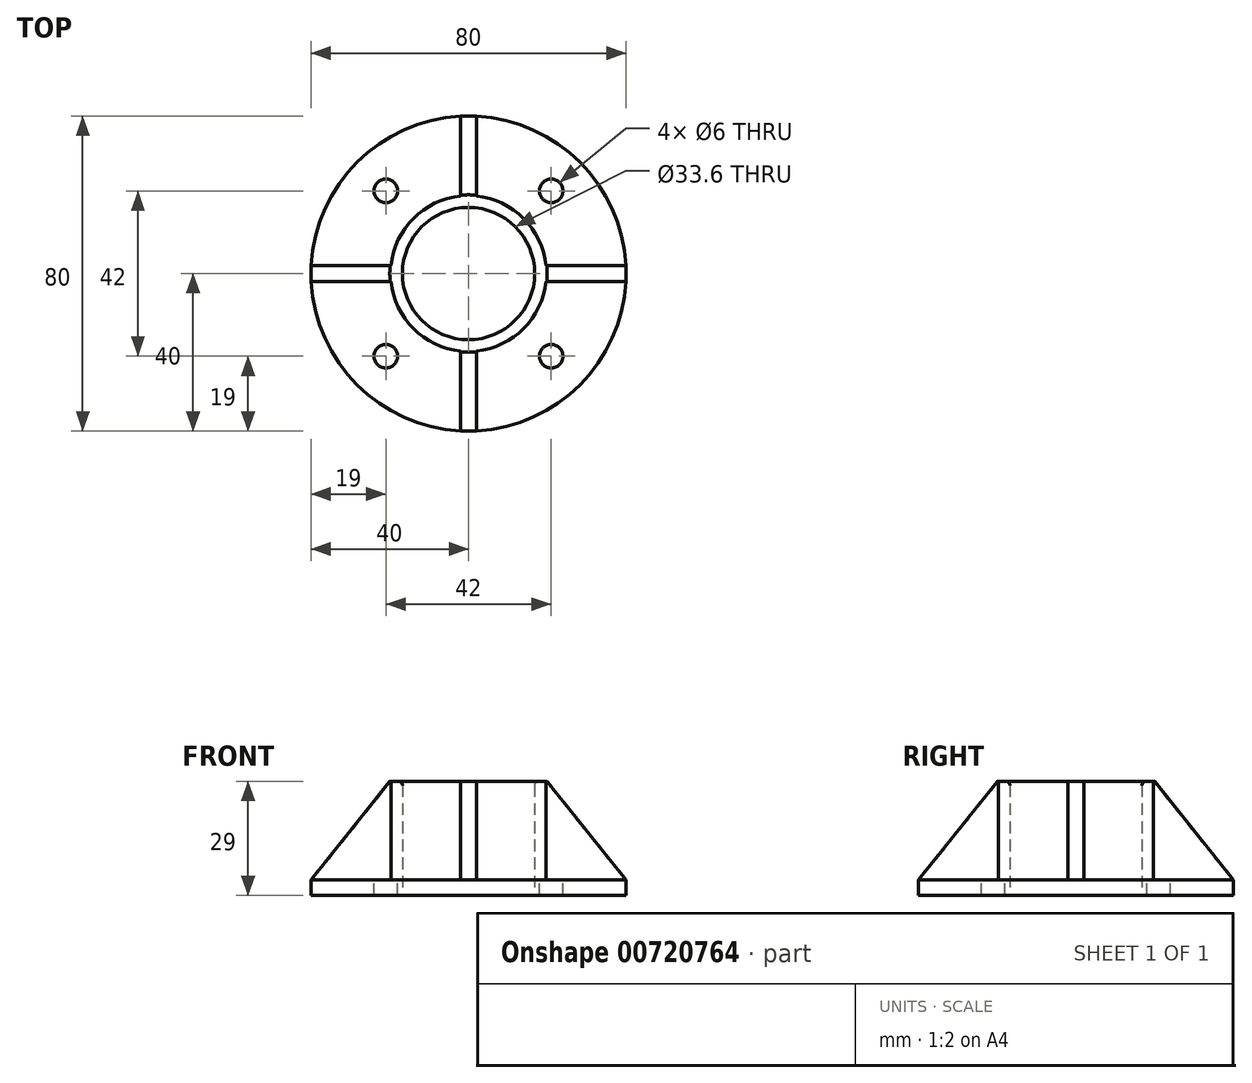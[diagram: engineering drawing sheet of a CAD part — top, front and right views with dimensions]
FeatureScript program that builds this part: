
annotation { "Feature Type Name" : "Feature", "Feature Type Description" : "" }
export const myFeature = defineFeature(function(context is Context, id is Id, definition is map)
    precondition{}
    {
        {
            var Q0;
            Q0=qCreatedBy(makeId("Top.planeOp"),FACE);
            var sketch = newSketch(context, id + "F0", { "sketchPlane" : qUnion([Q0])});
            skCircle(sketch, "E0", {"center": v(0, 0) * mm, "radius": 16.8 * mm});
            skCircle(sketch, "E1", {"center": v(0, 0) * mm, "radius": 19.8 * mm});
            skLineSegment(sketch, "E2.bottom", {"start": v(2, -40) * mm, "end": v(-2, -40) * mm});
            skLineSegment(sketch, "E2.top", {"start": v(2, 40) * mm, "end": v(-2, 40) * mm});
            skLineSegment(sketch, "E2.left", {"start": v(2, -40) * mm, "end": v(2, 40) * mm});
            skLineSegment(sketch, "E2.right", {"start": v(-2, -40) * mm, "end": v(-2, 40) * mm});
            skLineSegment(sketch, "E3.bottom", {"start": v(40, -2) * mm, "end": v(-40, -2) * mm});
            skLineSegment(sketch, "E3.top", {"start": v(40, 2) * mm, "end": v(-40, 2) * mm});
            skLineSegment(sketch, "E3.left", {"start": v(40, -2) * mm, "end": v(40, 2) * mm});
            skLineSegment(sketch, "E3.right", {"start": v(-40, -2) * mm, "end": v(-40, 2) * mm});
            skCircle(sketch, "E4", {"center": v(0, 0) * mm, "radius": 40 * mm});
            skLineSegment(sketch, "E5", {"start": v(-40, -2) * mm, "end": v(-2, -40) * mm, "construction": true});
            skLineSegment(sketch, "E6", {"start": v(2, -40) * mm, "end": v(40, -2) * mm, "construction": true});
            skLineSegment(sketch, "E7", {"start": v(40, 2) * mm, "end": v(2, 40) * mm, "construction": true});
            skLineSegment(sketch, "E8", {"start": v(-2, 40) * mm, "end": v(-40, 2) * mm, "construction": true});
            skCircle(sketch, "E9", {"center": v(21, 21) * mm, "radius": 3 * mm});
            skCircle(sketch, "E10", {"center": v(21, -21) * mm, "radius": 3 * mm});
            skCircle(sketch, "E11", {"center": v(-21, -21) * mm, "radius": 3 * mm});
            skCircle(sketch, "E12", {"center": v(-21, 21) * mm, "radius": 3 * mm});
            skSolve(sketch);
        }
        {
            var Q0;
            Q0=makeQuery(id+"F0.imprint","IMPRINT",FACE,{"disambiguationData":[TD([[makeQuery(id+"F0.imprint","IMPRINT",EDGE,{"derivedFrom":sQuery(id+"F0.wireOp",EDGE,"E0")}),-1.0]])]});
            var Q1;
            {var subQ1=sQuery(id+"F0.wireOp",EDGE,"E3.top");var subQ3=sQuery(id+"F0.wireOp",EDGE,"E1");var subQ4=makeQuery(id+"F0.imprint","INTERSECT",VERTEX,{"disambiguationData":[OD(1.0)],"derivedFrom":[subQ3,subQ1]});Q1=makeQuery(id+"F0.imprint","IMPRINT",FACE,{"disambiguationData":[TD([[makeQuery(id+"F0.imprint","IMPRINT",EDGE,{"disambiguationData":[TD([[subQ4,-1.0]])],"derivedFrom":subQ3}),-1.0]])]});}
            var Q2;
            {var subQ1=sQuery(id+"F0.wireOp",EDGE,"E2.right");var subQ3=sQuery(id+"F0.wireOp",EDGE,"E1");var subQ4=makeQuery(id+"F0.imprint","INTERSECT",VERTEX,{"disambiguationData":[OD(1.0)],"derivedFrom":[subQ3,subQ1]});Q2=makeQuery(id+"F0.imprint","IMPRINT",FACE,{"disambiguationData":[TD([[makeQuery(id+"F0.imprint","IMPRINT",EDGE,{"disambiguationData":[TD([[subQ4,-1.0]])],"derivedFrom":subQ3}),-1.0]])]});}
            var Q3;
            {var subQ1=sQuery(id+"F0.wireOp",EDGE,"E3.top");var subQ3=sQuery(id+"F0.wireOp",EDGE,"E1");var subQ4=makeQuery(id+"F0.imprint","INTERSECT",VERTEX,{"disambiguationData":[OD(0.0)],"derivedFrom":[subQ3,subQ1]});Q3=makeQuery(id+"F0.imprint","IMPRINT",FACE,{"disambiguationData":[TD([[makeQuery(id+"F0.imprint","IMPRINT",EDGE,{"disambiguationData":[TD([[subQ4,1.0]])],"derivedFrom":subQ3}),-1.0]])]});}
            var Q4;
            {var subQ3=sQuery(id+"F0.wireOp",EDGE,"E1");var subQ6=sQuery(id+"F0.wireOp",EDGE,"E2.left");var subQ8=makeQuery(id+"F0.imprint","INTERSECT",VERTEX,{"disambiguationData":[OD(0.0)],"derivedFrom":[subQ3,subQ6]});Q4=makeQuery(id+"F0.imprint","IMPRINT",FACE,{"disambiguationData":[TD([[makeQuery(id+"F0.imprint","IMPRINT",EDGE,{"disambiguationData":[TD([[subQ8,-1.0]])],"derivedFrom":subQ3}),-1.0]])]});}
            extrude(context, id + "F1", {"entities" : qUnion([Q0, Q1, Q2, Q3, Q4]), "depth" : 25 * mm, "offsetDistance" : 25 * mm});
        }
        {
            var Q0;
            Q0=makeQuery(id+"F0.imprint","IMPRINT",FACE,{"disambiguationData":[TD([[makeQuery(id+"F0.imprint","IMPRINT",EDGE,{"derivedFrom":sQuery(id+"F0.wireOp",EDGE,"E12")}),-1.0]])]});
            var Q1;
            Q1=makeQuery(id+"F0.imprint","IMPRINT",FACE,{"disambiguationData":[TD([[makeQuery(id+"F0.imprint","IMPRINT",EDGE,{"derivedFrom":sQuery(id+"F0.wireOp",EDGE,"E9")}),-1.0]])]});
            var Q2;
            {var subQ1=sQuery(id+"F0.wireOp",EDGE,"E3.top");var subQ3=sQuery(id+"F0.wireOp",EDGE,"E1");var subQ4=makeQuery(id+"F0.imprint","INTERSECT",VERTEX,{"disambiguationData":[OD(0.0)],"derivedFrom":[subQ3,subQ1]});Q2=makeQuery(id+"F0.imprint","IMPRINT",FACE,{"disambiguationData":[TD([[makeQuery(id+"F0.imprint","IMPRINT",EDGE,{"disambiguationData":[TD([[subQ4,1.0]])],"derivedFrom":subQ3}),-1.0]])]});}
            var Q3;
            {var subQ3=sQuery(id+"F0.wireOp",EDGE,"E1");var subQ6=sQuery(id+"F0.wireOp",EDGE,"E2.left");var subQ8=makeQuery(id+"F0.imprint","INTERSECT",VERTEX,{"disambiguationData":[OD(0.0)],"derivedFrom":[subQ3,subQ6]});Q3=makeQuery(id+"F0.imprint","IMPRINT",FACE,{"disambiguationData":[TD([[makeQuery(id+"F0.imprint","IMPRINT",EDGE,{"disambiguationData":[TD([[subQ8,-1.0]])],"derivedFrom":subQ3}),-1.0]])]});}
            var Q4;
            Q4=makeQuery(id+"F0.imprint","IMPRINT",FACE,{"disambiguationData":[TD([[makeQuery(id+"F0.imprint","IMPRINT",EDGE,{"derivedFrom":sQuery(id+"F0.wireOp",EDGE,"E10")}),-1.0]])]});
            var Q5;
            {var subQ0=sQuery(id+"F0.wireOp",EDGE,"E2.left");var subQ1=sQuery(id+"F0.wireOp",EDGE,"E0");var subQ2=makeQuery(id+"F0.imprint","INTERSECT",VERTEX,{"disambiguationData":[OD(1.0)],"derivedFrom":[subQ1,subQ0]});Q5=makeQuery(id+"F0.imprint","IMPRINT",FACE,{"disambiguationData":[TD([[makeQuery(id+"F0.imprint","IMPRINT",EDGE,{"disambiguationData":[TD([[subQ2,-1.0]])],"derivedFrom":subQ1}),-1.0]])]});}
            var Q6;
            {var subQ0=sQuery(id+"F0.wireOp",EDGE,"E3.top");var subQ1=sQuery(id+"F0.wireOp",EDGE,"E0");var subQ2=makeQuery(id+"F0.imprint","INTERSECT",VERTEX,{"disambiguationData":[OD(0.0)],"derivedFrom":[subQ1,subQ0]});Q6=makeQuery(id+"F0.imprint","IMPRINT",FACE,{"disambiguationData":[TD([[makeQuery(id+"F0.imprint","IMPRINT",EDGE,{"disambiguationData":[TD([[subQ2,1.0]])],"derivedFrom":subQ1}),-1.0]])]});}
            var Q7;
            {var subQ0=sQuery(id+"F0.wireOp",EDGE,"E2.left");var subQ1=sQuery(id+"F0.wireOp",EDGE,"E0");var subQ2=makeQuery(id+"F0.imprint","INTERSECT",VERTEX,{"disambiguationData":[OD(0.0)],"derivedFrom":[subQ1,subQ0]});Q7=makeQuery(id+"F0.imprint","IMPRINT",FACE,{"disambiguationData":[TD([[makeQuery(id+"F0.imprint","IMPRINT",EDGE,{"disambiguationData":[TD([[subQ2,1.0]])],"derivedFrom":subQ1}),-1.0]])]});}
            var Q8;
            {var subQ0=sQuery(id+"F0.wireOp",EDGE,"E2.right");var subQ1=sQuery(id+"F0.wireOp",EDGE,"E0");var subQ2=makeQuery(id+"F0.imprint","INTERSECT",VERTEX,{"disambiguationData":[OD(1.0)],"derivedFrom":[subQ1,subQ0]});Q8=makeQuery(id+"F0.imprint","IMPRINT",FACE,{"disambiguationData":[TD([[makeQuery(id+"F0.imprint","IMPRINT",EDGE,{"disambiguationData":[TD([[subQ2,-1.0]])],"derivedFrom":subQ1}),-1.0]])]});}
            var Q9;
            {var subQ1=sQuery(id+"F0.wireOp",EDGE,"E2.right");var subQ3=sQuery(id+"F0.wireOp",EDGE,"E1");var subQ4=makeQuery(id+"F0.imprint","INTERSECT",VERTEX,{"disambiguationData":[OD(1.0)],"derivedFrom":[subQ3,subQ1]});Q9=makeQuery(id+"F0.imprint","IMPRINT",FACE,{"disambiguationData":[TD([[makeQuery(id+"F0.imprint","IMPRINT",EDGE,{"disambiguationData":[TD([[subQ4,-1.0]])],"derivedFrom":subQ3}),-1.0]])]});}
            var Q10;
            {var subQ0=sQuery(id+"F0.wireOp",EDGE,"E3.bottom");var subQ1=sQuery(id+"F0.wireOp",EDGE,"E0");var subQ2=makeQuery(id+"F0.imprint","INTERSECT",VERTEX,{"disambiguationData":[OD(0.0)],"derivedFrom":[subQ1,subQ0]});Q10=makeQuery(id+"F0.imprint","IMPRINT",FACE,{"disambiguationData":[TD([[makeQuery(id+"F0.imprint","IMPRINT",EDGE,{"disambiguationData":[TD([[subQ2,-1.0]])],"derivedFrom":subQ1}),-1.0]])]});}
            var Q11;
            Q11=makeQuery(id+"F0.imprint","IMPRINT",FACE,{"disambiguationData":[TD([[makeQuery(id+"F0.imprint","IMPRINT",EDGE,{"derivedFrom":sQuery(id+"F0.wireOp",EDGE,"E11")}),-1.0]])]});
            var Q12;
            {var subQ1=sQuery(id+"F0.wireOp",EDGE,"E3.top");var subQ3=sQuery(id+"F0.wireOp",EDGE,"E1");var subQ4=makeQuery(id+"F0.imprint","INTERSECT",VERTEX,{"disambiguationData":[OD(1.0)],"derivedFrom":[subQ3,subQ1]});Q12=makeQuery(id+"F0.imprint","IMPRINT",FACE,{"disambiguationData":[TD([[makeQuery(id+"F0.imprint","IMPRINT",EDGE,{"disambiguationData":[TD([[subQ4,-1.0]])],"derivedFrom":subQ3}),-1.0]])]});}
            var Q13;
            {var subQ0=sQuery(id+"F0.wireOp",EDGE,"E3.top");var subQ1=sQuery(id+"F0.wireOp",EDGE,"E0");var subQ2=makeQuery(id+"F0.imprint","INTERSECT",VERTEX,{"disambiguationData":[OD(1.0)],"derivedFrom":[subQ1,subQ0]});Q13=makeQuery(id+"F0.imprint","IMPRINT",FACE,{"disambiguationData":[TD([[makeQuery(id+"F0.imprint","IMPRINT",EDGE,{"disambiguationData":[TD([[subQ2,-1.0]])],"derivedFrom":subQ1}),-1.0]])]});}
            var Q14;
            {var subQ0=sQuery(id+"F0.wireOp",EDGE,"E2.right");var subQ1=sQuery(id+"F0.wireOp",EDGE,"E0");var subQ2=makeQuery(id+"F0.imprint","INTERSECT",VERTEX,{"disambiguationData":[OD(0.0)],"derivedFrom":[subQ1,subQ0]});Q14=makeQuery(id+"F0.imprint","IMPRINT",FACE,{"disambiguationData":[TD([[makeQuery(id+"F0.imprint","IMPRINT",EDGE,{"disambiguationData":[TD([[subQ2,-1.0]])],"derivedFrom":subQ1}),-1.0]])]});}
            var Q15;
            {var subQ0=sQuery(id+"F0.wireOp",EDGE,"E2.left");var subQ1=sQuery(id+"F0.wireOp",EDGE,"E0");var subQ2=makeQuery(id+"F0.imprint","INTERSECT",VERTEX,{"disambiguationData":[OD(0.0)],"derivedFrom":[subQ1,subQ0]});Q15=makeQuery(id+"F0.imprint","IMPRINT",FACE,{"disambiguationData":[TD([[makeQuery(id+"F0.imprint","IMPRINT",EDGE,{"disambiguationData":[TD([[subQ2,-1.0]])],"derivedFrom":subQ1}),-1.0]])]});}
            extrude(context, id + "F2", {"entities" : qUnion([Q0, Q1, Q2, Q3, Q4, Q5, Q6, Q7, Q8, Q9, Q10, Q11, Q12, Q13, Q14, Q15]), "operationType" : NewBodyOperationType.ADD, "oppositeDirection" : true, "depth" : 4 * mm, "offsetDistance" : 25 * mm});
        }
        {
            var Q0;
            {var subQ0=sQuery(id+"F0.wireOp",EDGE,"E4");Q0=makeQuery(id+"F1.opExtrude","CAP_EDGE",EDGE,{"disambiguationData":[OSD([subQ0]),TDD([makeQuery(id+"F0.imprint","IMPRINT",EDGE,{"disambiguationData":[TD([[makeQuery(id+"F0.imprint","INTERSECT",VERTEX,{"disambiguationData":[OD(1.0)],"derivedFrom":[sQuery(id+"F0.wireOp",EDGE,"E3.top"),subQ0]}),-1.0]])],"derivedFrom":subQ0}),makeQuery(id+"F0.imprint","IMPRINT",EDGE,{"disambiguationData":[TD([[makeQuery(id+"F0.imprint","INTERSECT",VERTEX,{"disambiguationData":[OD(1.0)],"derivedFrom":[sQuery(id+"F0.wireOp",EDGE,"E3.bottom"),subQ0]}),1.0]])],"derivedFrom":subQ0})])],"isStart":false});}
            var Q1;
            {var subQ0=sQuery(id+"F0.wireOp",EDGE,"E4");var subQ1=makeQuery(id+"F0.imprint","INTERSECT",VERTEX,{"derivedFrom":[sQuery(id+"F0.wireOp",EDGE,"E2.bottom"),subQ0]});Q1=makeQuery(id+"F1.opExtrude","CAP_EDGE",EDGE,{"disambiguationData":[OSD([subQ0]),TDD([makeQuery(id+"F0.imprint","IMPRINT",EDGE,{"disambiguationData":[TD([[subQ1,1.0]])],"derivedFrom":subQ0}),makeQuery(id+"F0.imprint","IMPRINT",EDGE,{"disambiguationData":[TD([[subQ1,-1.0]])],"derivedFrom":subQ0})])],"isStart":false});}
            var Q2;
            {var subQ0=sQuery(id+"F0.wireOp",EDGE,"E4");Q2=makeQuery(id+"F1.opExtrude","CAP_EDGE",EDGE,{"disambiguationData":[OSD([subQ0]),TDD([makeQuery(id+"F0.imprint","IMPRINT",EDGE,{"disambiguationData":[TD([[makeQuery(id+"F0.imprint","INTERSECT",VERTEX,{"disambiguationData":[OD(0.0)],"derivedFrom":[sQuery(id+"F0.wireOp",EDGE,"E3.top"),subQ0]}),1.0]])],"derivedFrom":subQ0}),makeQuery(id+"F0.imprint","IMPRINT",EDGE,{"disambiguationData":[TD([[makeQuery(id+"F0.imprint","INTERSECT",VERTEX,{"disambiguationData":[OD(0.0)],"derivedFrom":[sQuery(id+"F0.wireOp",EDGE,"E3.bottom"),subQ0]}),-1.0]])],"derivedFrom":subQ0})])],"isStart":false});}
            var Q3;
            {var subQ0=sQuery(id+"F0.wireOp",EDGE,"E4");var subQ1=makeQuery(id+"F0.imprint","INTERSECT",VERTEX,{"derivedFrom":[sQuery(id+"F0.wireOp",EDGE,"E2.top"),subQ0]});Q3=makeQuery(id+"F1.opExtrude","CAP_EDGE",EDGE,{"disambiguationData":[OSD([subQ0]),TDD([makeQuery(id+"F0.imprint","IMPRINT",EDGE,{"disambiguationData":[TD([[subQ1,1.0]])],"derivedFrom":subQ0}),makeQuery(id+"F0.imprint","IMPRINT",EDGE,{"disambiguationData":[TD([[subQ1,-1.0]])],"derivedFrom":subQ0})])],"isStart":false});}
            chamfer(context, id + "F3", {"entities" : qUnion([Q0, Q1, Q2, Q3]), "chamferType" : ChamferType.TWO_OFFSETS, "width1" : 20 * mm, "oppositeDirection" : false, "width2" : 25 * mm, "tangentPropagation" : true});
        }
        {
            var Q0;
            Q0=makeQuery(id+"F1.opExtrude","CAP_EDGE",EDGE,{"disambiguationData":[OSD([sQuery(id+"F0.wireOp",EDGE,"E0")])],"isStart":false});
            fillet(context, id + "F4", {"entities" : qUnion([Q0]), "radius" : 1 * mm, "tangentPropagation" : true, "allowEdgeOverflow" : false});
        }
    });
